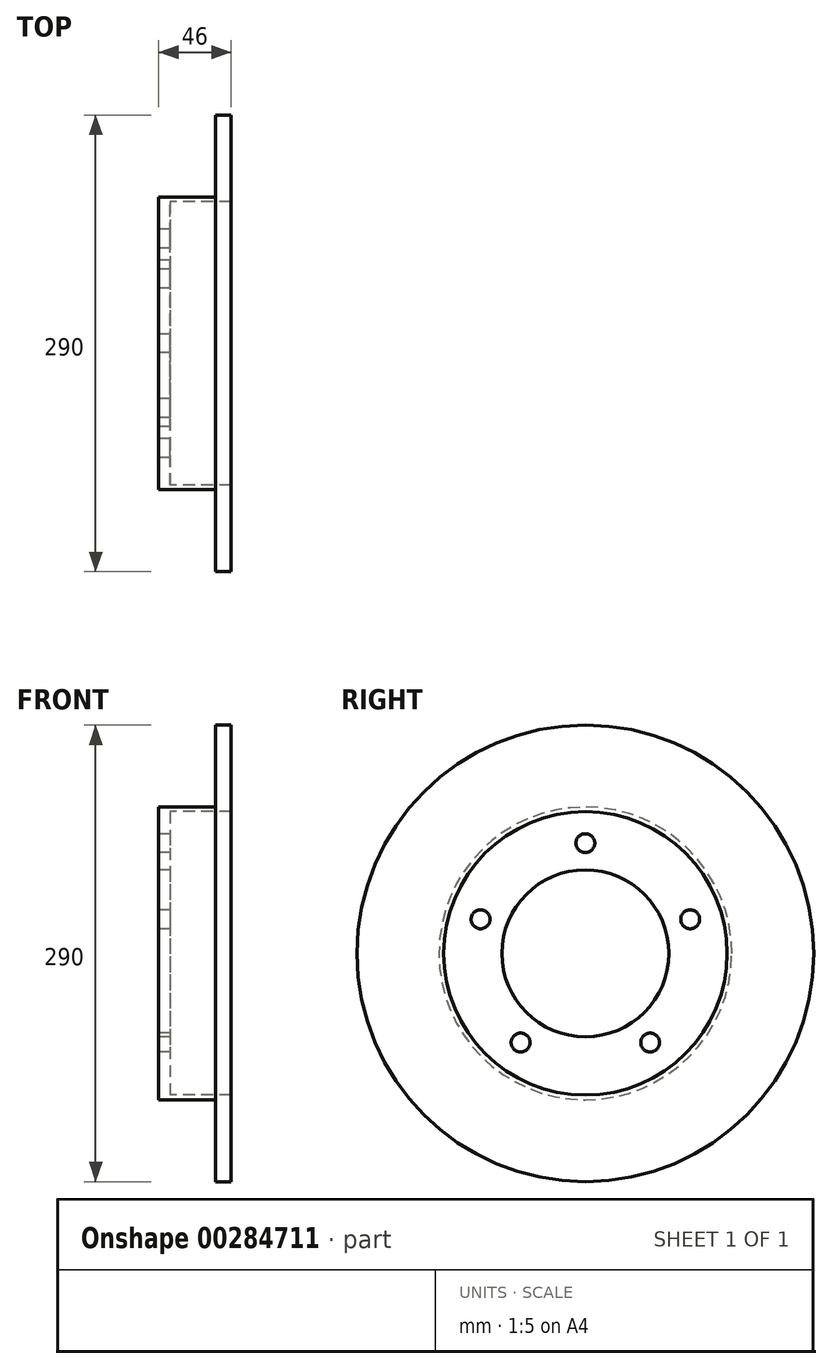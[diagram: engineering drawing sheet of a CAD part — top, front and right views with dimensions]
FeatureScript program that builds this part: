
annotation { "Feature Type Name" : "Feature", "Feature Type Description" : "" }
export const myFeature = defineFeature(function(context is Context, id is Id, definition is map)
    precondition{}
    {
        {
            var Q0;
            Q0=qCreatedBy(makeId("Front.planeOp"),FACE);
            var sketch = newSketch(context, id + "F0", { "sketchPlane" : qUnion([Q0])});
            skLineSegment(sketch, "E0", {"start": v(0, 0) * mm, "end": v(0, 145) * mm, "construction": true});
            skLineSegment(sketch, "E1", {"start": v(0, 145) * mm, "end": v(-10, 145) * mm});
            skLineSegment(sketch, "E2", {"start": v(-10, 145) * mm, "end": v(-10, 90) * mm});
            skLineSegment(sketch, "E3", {"start": v(-10, 90) * mm, "end": v(-46, 90) * mm});
            skLineSegment(sketch, "E4", {"start": v(-46, 90) * mm, "end": v(-46, 0) * mm});
            skLineSegment(sketch, "E5", {"start": v(-46, 0) * mm, "end": v(-38.7, 0) * mm});
            skLineSegment(sketch, "E6", {"start": v(-38.7, 0) * mm, "end": v(-38.7, 90) * mm});
            skLineSegment(sketch, "E7", {"start": v(-38.7, 0) * mm, "end": v(0, 0) * mm});
            skLineSegment(sketch, "E8", {"start": v(-46, 90) * mm, "end": v(-46, 93) * mm});
            skLineSegment(sketch, "E9", {"start": v(-46, 93) * mm, "end": v(-10, 93) * mm});
            skLineSegment(sketch, "E10", {"start": v(-10, 90) * mm, "end": v(0, 90) * mm});
            skLineSegment(sketch, "E11", {"start": v(0, 145) * mm, "end": v(0, 90) * mm});
            skSolve(sketch);
        }
        {
            var Q0;
            {var subQ0=sQuery(id+"F0.wireOp",EDGE,"E4");Q0=makeQuery(id+"F0.imprint","IMPRINT",FACE,{"disambiguationData":[TD([[makeQuery(id+"F0.imprint","IMPRINT",EDGE,{"derivedFrom":subQ0}),1.0]])]});}
            var Q1;
            {var subQ0=sQuery(id+"F0.wireOp",EDGE,"E8");Q1=makeQuery(id+"F0.imprint","IMPRINT",FACE,{"disambiguationData":[TD([[makeQuery(id+"F0.imprint","IMPRINT",EDGE,{"derivedFrom":subQ0}),-1.0]])]});}
            var Q2;
            {var subQ3=sQuery(id+"F0.wireOp",EDGE,"E1");Q2=makeQuery(id+"F0.imprint","IMPRINT",FACE,{"disambiguationData":[TD([[makeQuery(id+"F0.imprint","IMPRINT",EDGE,{"derivedFrom":subQ3}),1.0]])]});}
            var Q3;
            Q3=sQuery(id+"F0.wireOp",EDGE,"E0");
            var Q4;
            Q4=sQuery(id+"F0.wireOp",EDGE,"E7");
            revolve(context, id + "F1", {"entities" : qUnion([Q0, Q1, Q2]), "surfaceEntities" : qUnion([Q3]), "axis" : qUnion([Q4]), "revolveType" : RevolveType.FULL});
        }
        {
            var Q0;
            Q0=makeQuery(id+"F1.opRevolve","SWEPT_FACE",FACE,{"disambiguationData":[OSD([sQuery(id+"F0.wireOp",EDGE,"E4"),sQuery(id+"F0.wireOp",EDGE,"E8")])]});
            var sketch = newSketch(context, id + "F2", { "sketchPlane" : qUnion([Q0])});
            skCircle(sketch, "E12", {"center": v(0, 0) * mm, "radius": 53 * mm});
            skPoint(sketch, "E13", {"position": v(0, 70) * mm});
            skCircle(sketch, "E14", {"center": v(0, 70) * mm, "radius": 6 * mm});
            skCircle(sketch, "E15.1.0", {"center": v(-66.57, 21.63) * mm, "radius": 6 * mm});
            skCircle(sketch, "E15.2.0", {"center": v(-41.14, -56.63) * mm, "radius": 6 * mm});
            skCircle(sketch, "E15.3.0", {"center": v(41.14, -56.63) * mm, "radius": 6 * mm});
            skCircle(sketch, "E15.4.0", {"center": v(66.57, 21.63) * mm, "radius": 6 * mm});
            skSolve(sketch);
        }
        {
            var Q0;
            Q0=qSketchRegion(id+"F2",true);
            extrude(context, id + "F3", {"entities" : qUnion([Q0]), "operationType" : NewBodyOperationType.REMOVE, "oppositeDirection" : true, "depth" : 7.3 * mm});
        }
    });
